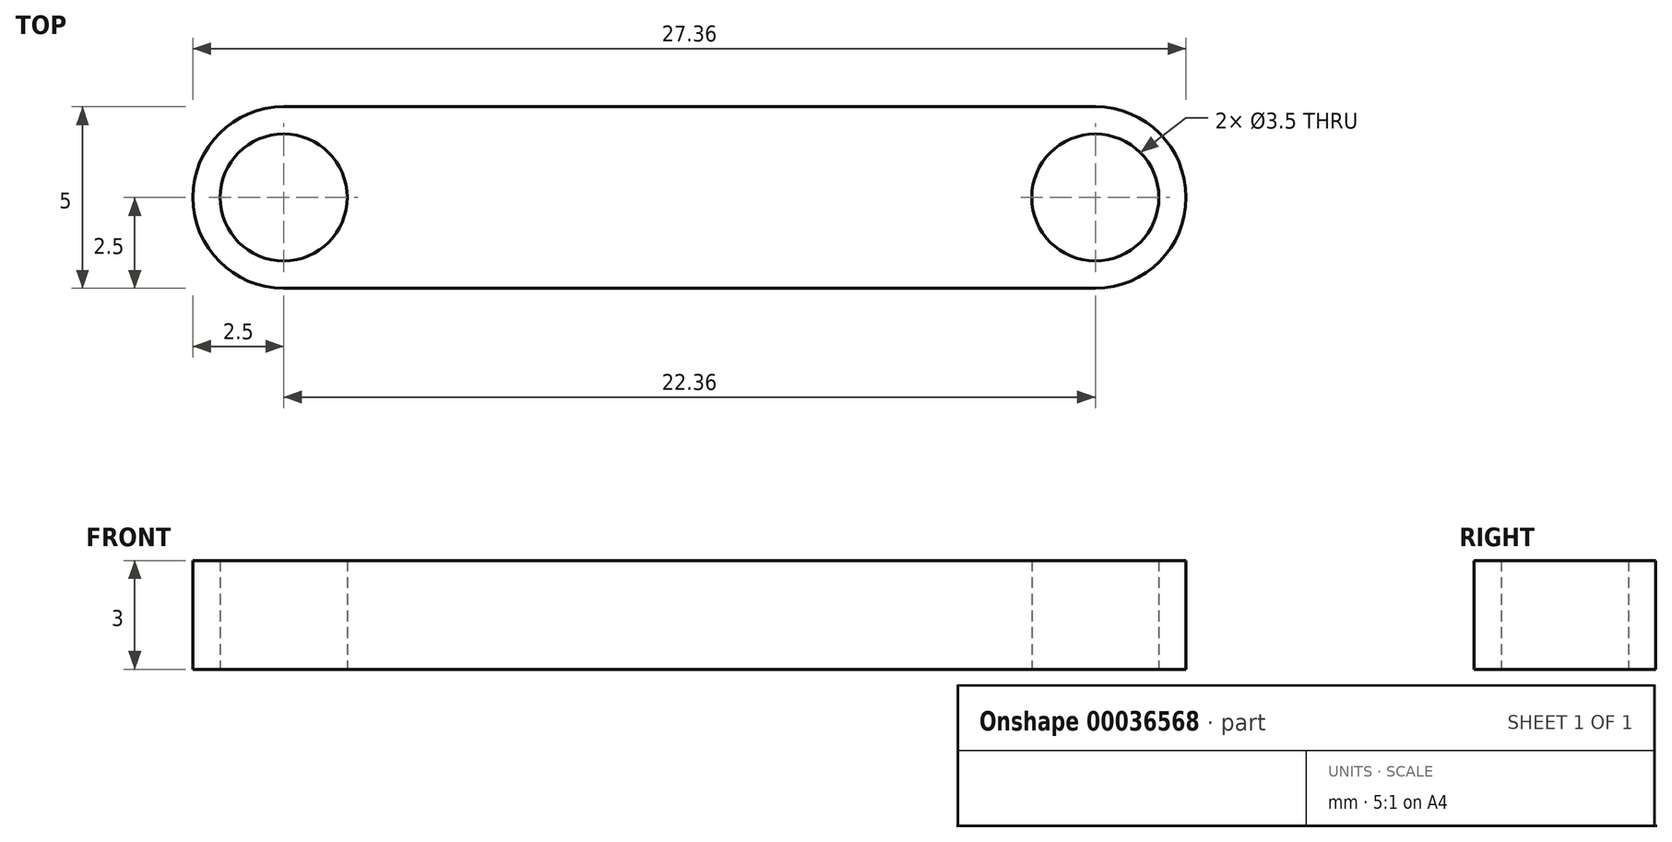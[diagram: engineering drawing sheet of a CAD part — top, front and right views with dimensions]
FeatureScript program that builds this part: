
annotation { "Feature Type Name" : "Feature", "Feature Type Description" : "" }
export const myFeature = defineFeature(function(context is Context, id is Id, definition is map)
    precondition{}
    {
        {
            var Q0;
            Q0=qCreatedBy(makeId("Top.planeOp"),FACE);
            var sketch = newSketch(context, id + "F0", { "sketchPlane" : qUnion([Q0])});
            skLineSegment(sketch, "E0.bottom", {"start": v(-11.18, 2.5) * mm, "end": v(11.18, 2.5) * mm});
            skLineSegment(sketch, "E0.top", {"start": v(-11.18, -2.5) * mm, "end": v(11.18, -2.5) * mm});
            skArc(sketch, "E1", {"start": v(-11.18, 2.5) * mm, "mid": v(-13.68, 0) * mm, "end": v(-11.18, -2.5) * mm});
            skArc(sketch, "E2", {"start": v(11.18, -2.5) * mm, "mid": v(13.68, 0) * mm, "end": v(11.18, 2.5) * mm});
            skCircle(sketch, "E3", {"center": v(-11.18, 0) * mm, "radius": 1.75 * mm});
            skCircle(sketch, "E4", {"center": v(11.18, 0) * mm, "radius": 1.75 * mm});
            skSolve(sketch);
        }
        {
            var Q0;
            Q0 = qSketchRegion(id + "F0", true);
            extrude(context, id + "F1", {"entities" : qUnion([Q0]), "depth" : 3 * mm});
        }
    });
